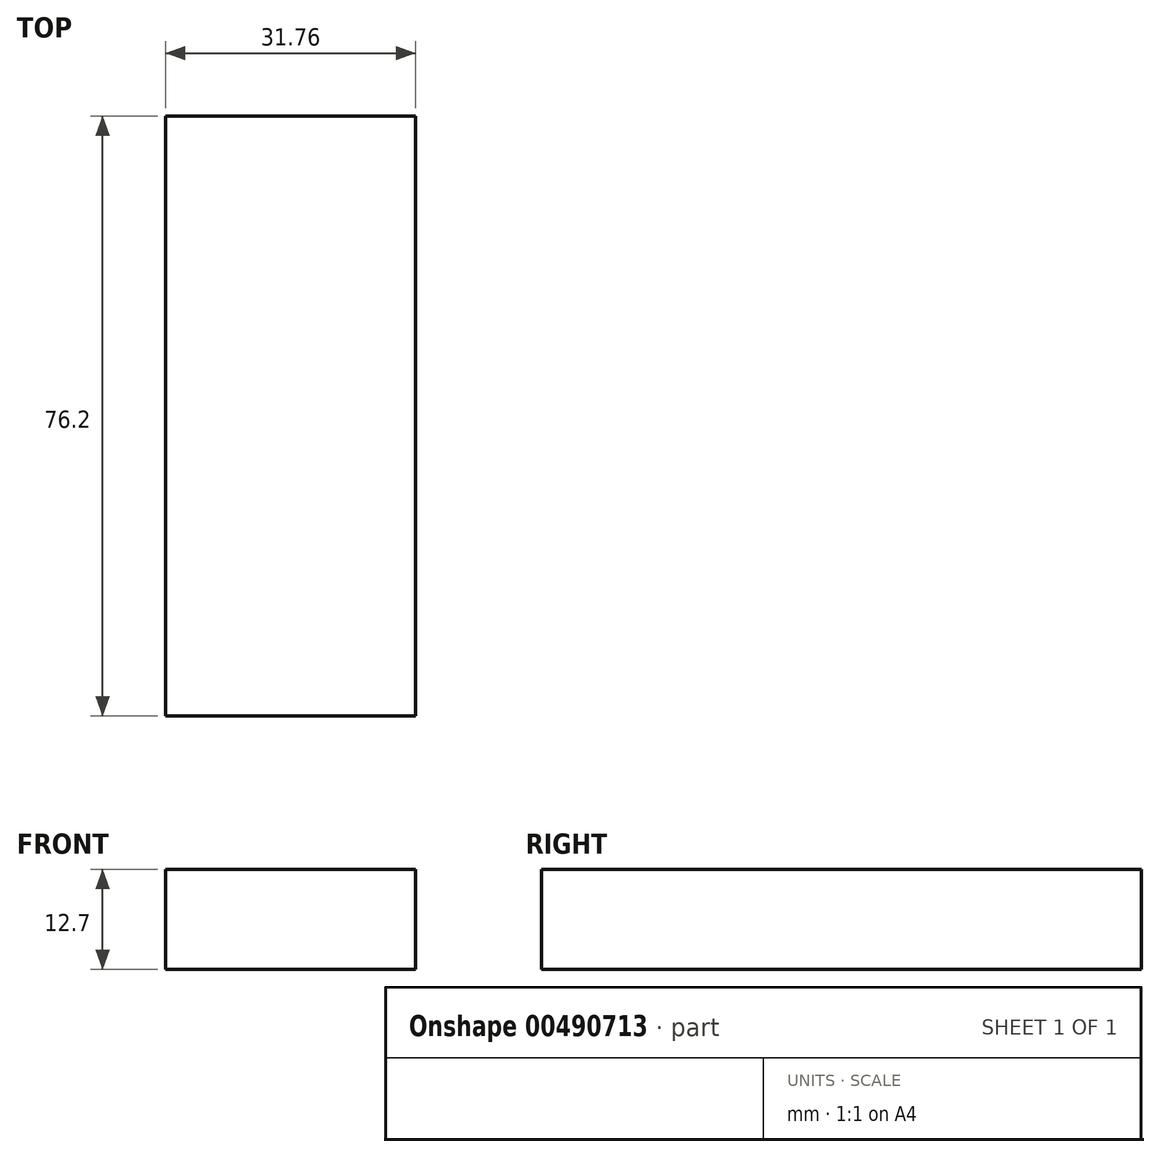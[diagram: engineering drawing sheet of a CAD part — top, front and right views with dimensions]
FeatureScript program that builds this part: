
annotation { "Feature Type Name" : "Feature", "Feature Type Description" : "" }
export const myFeature = defineFeature(function(context is Context, id is Id, definition is map)
    precondition{}
    {
        {
            var Q0;
            Q0=qCreatedBy(makeId("Top.planeOp"),FACE);
            var sketch = newSketch(context, id + "F0", { "sketchPlane" : qUnion([Q0])});
            skLineSegment(sketch, "E0.bottom", {"start": v(15.88, 38.1) * mm, "end": v(-15.87, 38.1) * mm});
            skLineSegment(sketch, "E0.top", {"start": v(15.87, -38.1) * mm, "end": v(-15.88, -38.1) * mm});
            skLineSegment(sketch, "E0.left", {"start": v(15.88, 38.1) * mm, "end": v(15.87, -38.1) * mm});
            skLineSegment(sketch, "E0.right", {"start": v(-15.87, 38.1) * mm, "end": v(-15.88, -38.1) * mm});
            skPoint(sketch, "E0.middle", {"position": v(0, 0) * mm});
            skSolve(sketch);
        }
        {
            var Q0;
            Q0 = qSketchRegion(id + "F0", true);
            extrude(context, id + "F1", {"entities" : qUnion([Q0]), "depth" : 12.7 * mm});
        }
    });
